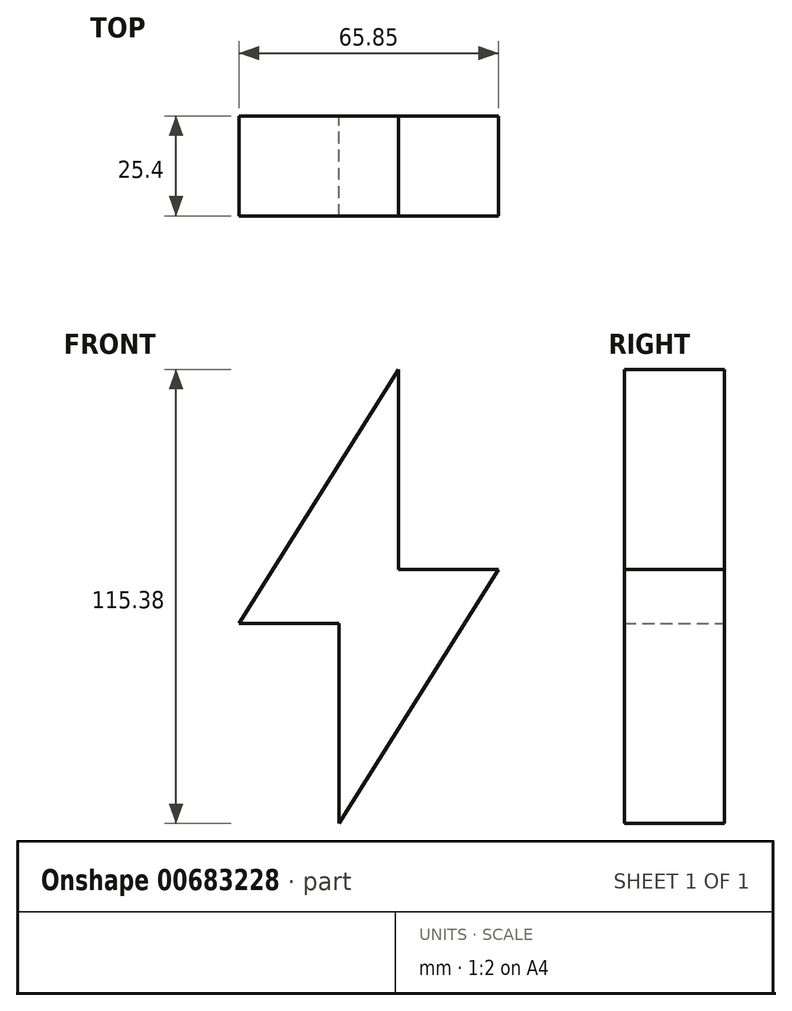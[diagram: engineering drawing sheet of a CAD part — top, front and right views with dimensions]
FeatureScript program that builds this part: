
annotation { "Feature Type Name" : "Feature", "Feature Type Description" : "" }
export const myFeature = defineFeature(function(context is Context, id is Id, definition is map)
    precondition{}
    {
        {
            var Q0;
            Q0=qCreatedBy(makeId("Front.planeOp"),FACE);
            var sketch = newSketch(context, id + "F0", { "sketchPlane" : qUnion([Q0])});
            skLineSegment(sketch, "E0", {"start": v(29.97, 45.38) * mm, "end": v(29.97, -5.42) * mm});
            skLineSegment(sketch, "E1", {"start": v(29.97, -5.42) * mm, "end": v(55.37, -5.42) * mm});
            skLineSegment(sketch, "E2", {"start": v(55.37, -5.42) * mm, "end": v(14.92, -70) * mm});
            skLineSegment(sketch, "E3", {"start": v(14.92, -70) * mm, "end": v(14.92, -19.2) * mm});
            skLineSegment(sketch, "E4", {"start": v(14.92, -19.2) * mm, "end": v(-10.48, -19.2) * mm});
            skLineSegment(sketch, "E5", {"start": v(-10.48, -19.2) * mm, "end": v(29.97, 45.38) * mm});
            skSolve(sketch);
        }
        {
            var Q0;
            Q0=makeQuery(id+"F0.imprint","IMPRINT",FACE,{"disambiguationData":[TD([[makeQuery(id+"F0.imprint","IMPRINT",EDGE,{"derivedFrom":sQuery(id+"F0.wireOp",EDGE,"E0")}),-1.0]])]});
            extrude(context, id + "F1", {"entities" : qUnion([Q0]), "depth" : 25.4 * mm, "offsetDistance" : 25.4 * mm});
        }
    });
